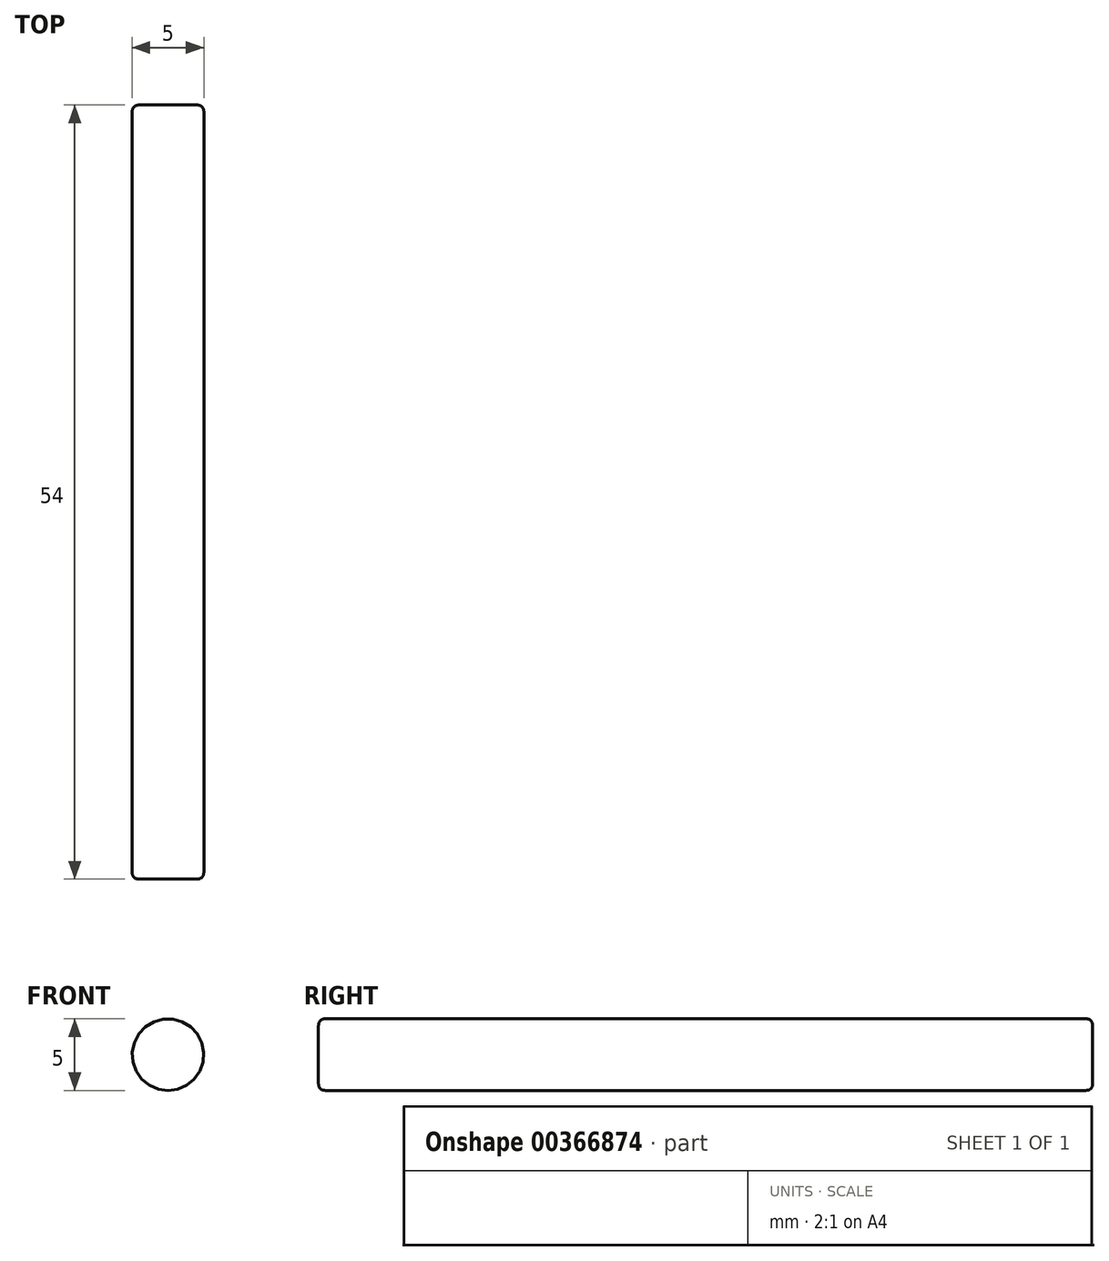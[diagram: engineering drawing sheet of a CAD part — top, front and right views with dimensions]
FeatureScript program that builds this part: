
annotation { "Feature Type Name" : "Feature", "Feature Type Description" : "" }
export const myFeature = defineFeature(function(context is Context, id is Id, definition is map)
    precondition{}
    {
        {
            var Q0;
            Q0=qCreatedBy(makeId("Front.planeOp"),FACE);
            var sketch = newSketch(context, id + "F0", { "sketchPlane" : qUnion([Q0])});
            skCircle(sketch, "E0", {"center": v(-51.34, 40.76) * mm, "radius": 2.5 * mm});
            skSolve(sketch);
        }
        {
            var Q0;
            Q0=makeQuery(id+"F0.imprint","IMPRINT",FACE,{"disambiguationData":[TD([[makeQuery(id+"F0.imprint","IMPRINT",EDGE,{"derivedFrom":sQuery(id+"F0.wireOp",EDGE,"E0")}),1.0]])]});
            extrude(context, id + "F1", {"entities" : qUnion([Q0]), "depth" : 54 * mm});
        }
        {
            var Q0;
            Q0=makeQuery(id+"F1.opExtrude","CAP_EDGE",EDGE,{"disambiguationData":[OSD([sQuery(id+"F0.wireOp",EDGE,"E0")])],"isStart":false});
            fillet(context, id + "F2", {"entities" : qUnion([Q0]), "radius" : .5 * mm, "rho" : 0.5, "crossSection" : FilletCrossSection.CONIC, "allowEdgeOverflow" : false});
        }
        {
            var Q0;
            Q0=makeQuery(id+"F1.opExtrude","CAP_EDGE",EDGE,{"disambiguationData":[OSD([sQuery(id+"F0.wireOp",EDGE,"E0")])],"isStart":true});
            fillet(context, id + "F3", {"entities" : qUnion([Q0]), "radius" : .5 * mm, "rho" : 0.5, "crossSection" : FilletCrossSection.CONIC, "allowEdgeOverflow" : false});
        }
    });
